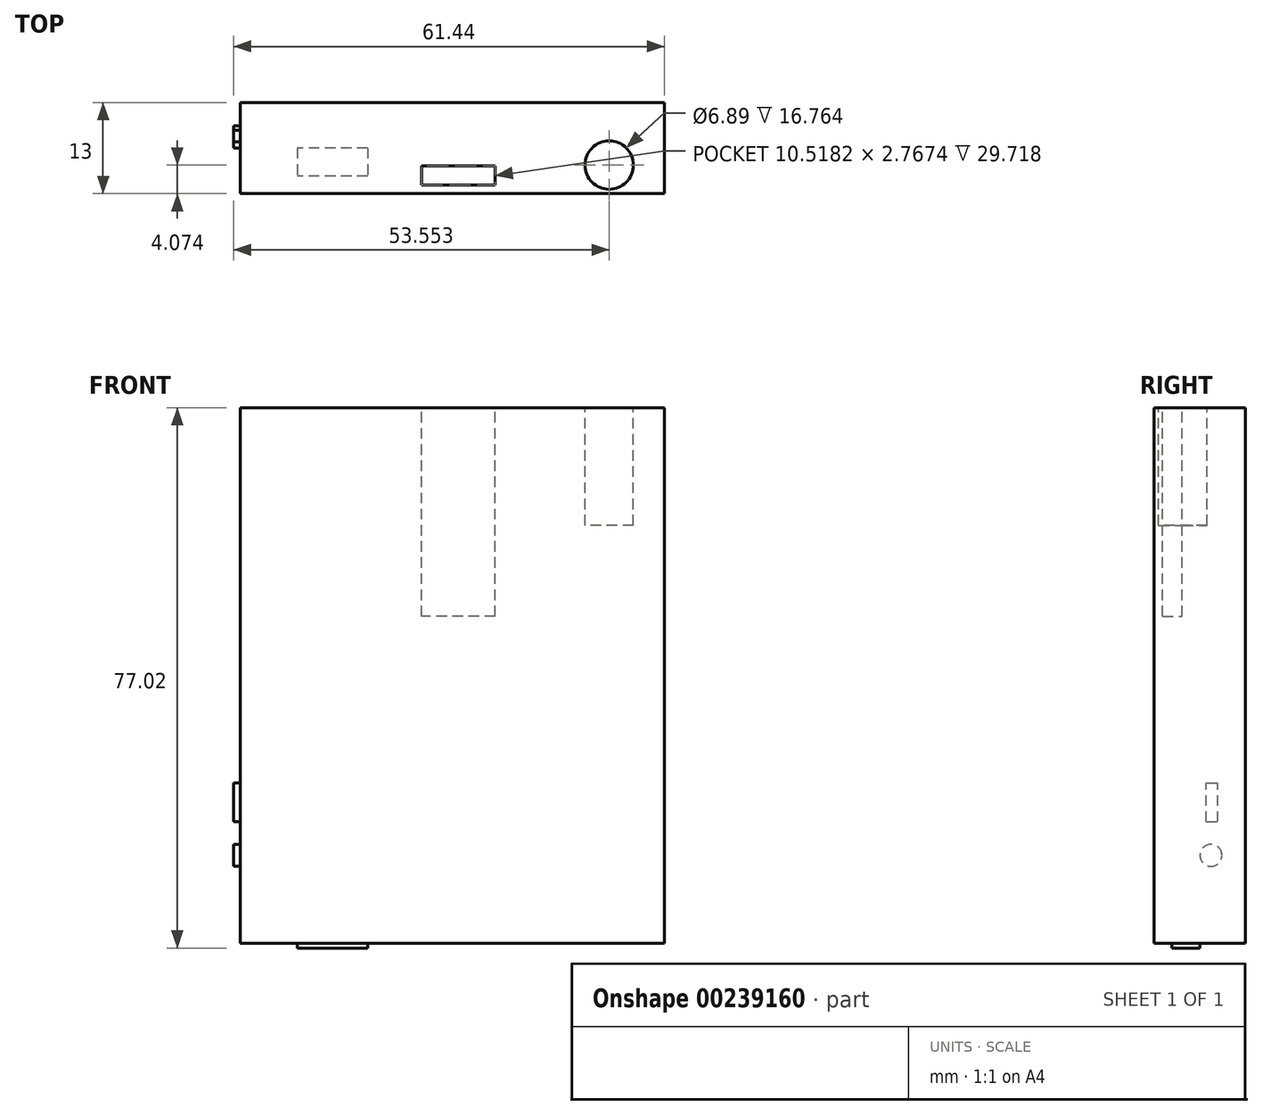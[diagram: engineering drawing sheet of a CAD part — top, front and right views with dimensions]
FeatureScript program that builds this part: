
annotation { "Feature Type Name" : "Feature", "Feature Type Description" : "" }
export const myFeature = defineFeature(function(context is Context, id is Id, definition is map)
    precondition{}
    {
        {
            var Q0;
            Q0=qCreatedBy(makeId("Front.planeOp"),FACE);
            var sketch = newSketch(context, id + "F0", { "sketchPlane" : qUnion([Q0])});
            skLineSegment(sketch, "E0.bottom", {"start": v(-30.22, 38.16) * mm, "end": v(30.22, 38.16) * mm});
            skLineSegment(sketch, "E0.top", {"start": v(-30.22, -38.16) * mm, "end": v(30.22, -38.16) * mm});
            skLineSegment(sketch, "E0.left", {"start": v(-30.22, 38.16) * mm, "end": v(-30.22, -38.16) * mm});
            skLineSegment(sketch, "E0.right", {"start": v(30.22, 38.16) * mm, "end": v(30.22, -38.16) * mm});
            skPoint(sketch, "E0.middle", {"position": v(0, 0) * mm});
            skSolve(sketch);
        }
        {
            var Q0;
            Q0 = qSketchRegion(id + "F0", true);
            extrude(context, id + "F1", {"entities" : qUnion([Q0]), "depth" : 13 * mm});
        }
        {
            var Q0;
            Q0=makeQuery(id+"F1.opExtrude","CAP_FACE",FACE,{"disambiguationData":[OSD([sQuery(id+"F0.wireOp",EDGE,"E0.bottom"),sQuery(id+"F0.wireOp",EDGE,"E0.top"),sQuery(id+"F0.wireOp",EDGE,"E0.left"),sQuery(id+"F0.wireOp",EDGE,"E0.right")])],"isStart":true});
            var sketch = newSketch(context, id + "F2", { "sketchPlane" : qUnion([Q0])});
            skCircle(sketch, "E1", {"center": v(-20.47, 49.87) * mm, "radius": 4.5 * mm});
            skSolve(sketch);
        }
        {
            var Q0;
            Q0 = qSketchRegion(id + "F2", true);
            extrude(context, id + "F3", {"entities" : qUnion([Q0]), "operationType" : NewBodyOperationType.REMOVE, "depth" : 7.87 * mm});
        }
        {
            var Q0;
            Q0=makeQuery(id+"F1.opExtrude","SWEPT_FACE",FACE,{"disambiguationData":[OSD([sQuery(id+"F0.wireOp",EDGE,"E0.bottom")])]});
            var sketch = newSketch(context, id + "F4", { "sketchPlane" : qUnion([Q0])});
            skCircle(sketch, "E2", {"center": v(22.33, -8.93) * mm, "radius": 3.45 * mm});
            skSolve(sketch);
        }
        {
            var Q0;
            Q0 = qSketchRegion(id + "F4", true);
            extrude(context, id + "F5", {"entities" : qUnion([Q0]), "operationType" : NewBodyOperationType.REMOVE, "oppositeDirection" : true, "depth" : 16.76 * mm});
        }
        {
            var Q0;
            Q0=makeQuery(id+"F1.opExtrude","SWEPT_FACE",FACE,{"disambiguationData":[OSD([sQuery(id+"F0.wireOp",EDGE,"E0.top")])]});
            var sketch = newSketch(context, id + "F6", { "sketchPlane" : qUnion([Q0])});
            skLineSegment(sketch, "E3.bottom", {"start": v(-12.09, 6.49) * mm, "end": v(-22.09, 6.49) * mm});
            skLineSegment(sketch, "E3.top", {"start": v(-12.09, 10.5) * mm, "end": v(-22.09, 10.5) * mm});
            skLineSegment(sketch, "E3.left", {"start": v(-12.09, 6.49) * mm, "end": v(-12.09, 10.5) * mm});
            skLineSegment(sketch, "E3.right", {"start": v(-22.09, 6.49) * mm, "end": v(-22.09, 10.5) * mm});
            skSolve(sketch);
        }
        {
            var Q0;
            Q0 = qSketchRegion(id + "F6", true);
            extrude(context, id + "F7", {"entities" : qUnion([Q0]), "operationType" : NewBodyOperationType.ADD, "depth" : 0.7 * mm});
        }
        {
            var Q0;
            Q0=makeQuery(id+"F1.opExtrude","SWEPT_FACE",FACE,{"disambiguationData":[OSD([sQuery(id+"F0.wireOp",EDGE,"E0.bottom")])]});
            var sketch = newSketch(context, id + "F8", { "sketchPlane" : qUnion([Q0])});
            skLineSegment(sketch, "E4.bottom", {"start": v(6.52, -11.63) * mm, "end": v(-5.57, -11.63) * mm});
            skLineSegment(sketch, "E4.top", {"start": v(6.52, -9.32) * mm, "end": v(-5.57, -9.32) * mm});
            skLineSegment(sketch, "E4.left", {"start": v(6.52, -11.63) * mm, "end": v(6.52, -9.32) * mm});
            skLineSegment(sketch, "E4.right", {"start": v(-5.57, -11.63) * mm, "end": v(-5.57, -9.32) * mm});
            skSolve(sketch);
        }
        {
            var Q0;
            Q0 = qSketchRegion(id + "F8", true);
            extrude(context, id + "F9", {"entities" : qUnion([Q0]), "operationType" : NewBodyOperationType.ADD, "oppositeDirection" : true, "depth" : 7.87 * mm});
        }
        {
            var Q0;
            Q0=makeQuery(id+"F1.opExtrude","SWEPT_FACE",FACE,{"disambiguationData":[OSD([sQuery(id+"F0.wireOp",EDGE,"E0.bottom")])]});
            var sketch = newSketch(context, id + "F10", { "sketchPlane" : qUnion([Q0])});
            skLineSegment(sketch, "E5.bottom", {"start": v(3.71, -10.32) * mm, "end": v(-6.29, -10.32) * mm});
            skLineSegment(sketch, "E5.top", {"start": v(3.71, -7.65) * mm, "end": v(-6.29, -7.65) * mm});
            skLineSegment(sketch, "E5.left", {"start": v(3.71, -10.32) * mm, "end": v(3.71, -7.65) * mm});
            skLineSegment(sketch, "E5.right", {"start": v(-6.29, -10.32) * mm, "end": v(-6.29, -7.65) * mm});
            skSolve(sketch);
        }
        {
            var Q0;
            Q0 = qSketchRegion(id + "F10", true);
            extrude(context, id + "F11", {"entities" : qUnion([Q0]), "operationType" : NewBodyOperationType.ADD, "oppositeDirection" : true, "depth" : 8.64 * mm});
        }
        {
            var Q0;
            Q0=makeQuery(id+"F1.opExtrude","SWEPT_FACE",FACE,{"disambiguationData":[OSD([sQuery(id+"F0.wireOp",EDGE,"E0.bottom")])]});
            var sketch = newSketch(context, id + "F12", { "sketchPlane" : qUnion([Q0])});
            skLineSegment(sketch, "E6.bottom", {"start": v(6.1, -11.8) * mm, "end": v(-4.43, -11.8) * mm});
            skLineSegment(sketch, "E6.top", {"start": v(6.1, -9.03) * mm, "end": v(-4.43, -9.03) * mm});
            skLineSegment(sketch, "E6.left", {"start": v(6.1, -11.8) * mm, "end": v(6.1, -9.03) * mm});
            skLineSegment(sketch, "E6.right", {"start": v(-4.43, -11.8) * mm, "end": v(-4.43, -9.03) * mm});
            skSolve(sketch);
        }
        {
            var Q0;
            Q0 = qSketchRegion(id + "F12", true);
            extrude(context, id + "F13", {"entities" : qUnion([Q0]), "operationType" : NewBodyOperationType.REMOVE, "oppositeDirection" : true, "depth" : 29.72 * mm});
        }
        {
            var Q0;
            Q0=makeQuery(id+"F1.opExtrude","SWEPT_FACE",FACE,{"disambiguationData":[OSD([sQuery(id+"F0.wireOp",EDGE,"E0.left")])]});
            var sketch = newSketch(context, id + "F14", { "sketchPlane" : qUnion([Q0])});
            skCircle(sketch, "E7", {"center": v(4.9, -25.65) * mm, "radius": 1.57 * mm});
            skSolve(sketch);
        }
        {
            var Q0;
            Q0 = qSketchRegion(id + "F14", true);
            extrude(context, id + "F15", {"entities" : qUnion([Q0]), "operationType" : NewBodyOperationType.ADD, "depth" : 1 * mm});
        }
        {
            var Q0;
            Q0=makeQuery(id+"F1.opExtrude","SWEPT_FACE",FACE,{"disambiguationData":[OSD([sQuery(id+"F0.wireOp",EDGE,"E0.left")])]});
            var sketch = newSketch(context, id + "F16", { "sketchPlane" : qUnion([Q0])});
            skLineSegment(sketch, "E8.bottom", {"start": v(5.59, -20.88) * mm, "end": v(3.96, -20.88) * mm});
            skLineSegment(sketch, "E8.top", {"start": v(5.59, -15.3) * mm, "end": v(3.96, -15.3) * mm});
            skLineSegment(sketch, "E8.left", {"start": v(5.59, -20.88) * mm, "end": v(5.59, -15.3) * mm});
            skLineSegment(sketch, "E8.right", {"start": v(3.96, -20.88) * mm, "end": v(3.96, -15.3) * mm});
            skSolve(sketch);
        }
        {
            var Q0;
            Q0 = qSketchRegion(id + "F16", true);
            extrude(context, id + "F17", {"entities" : qUnion([Q0]), "operationType" : NewBodyOperationType.ADD, "depth" : 1 * mm});
        }
    });
